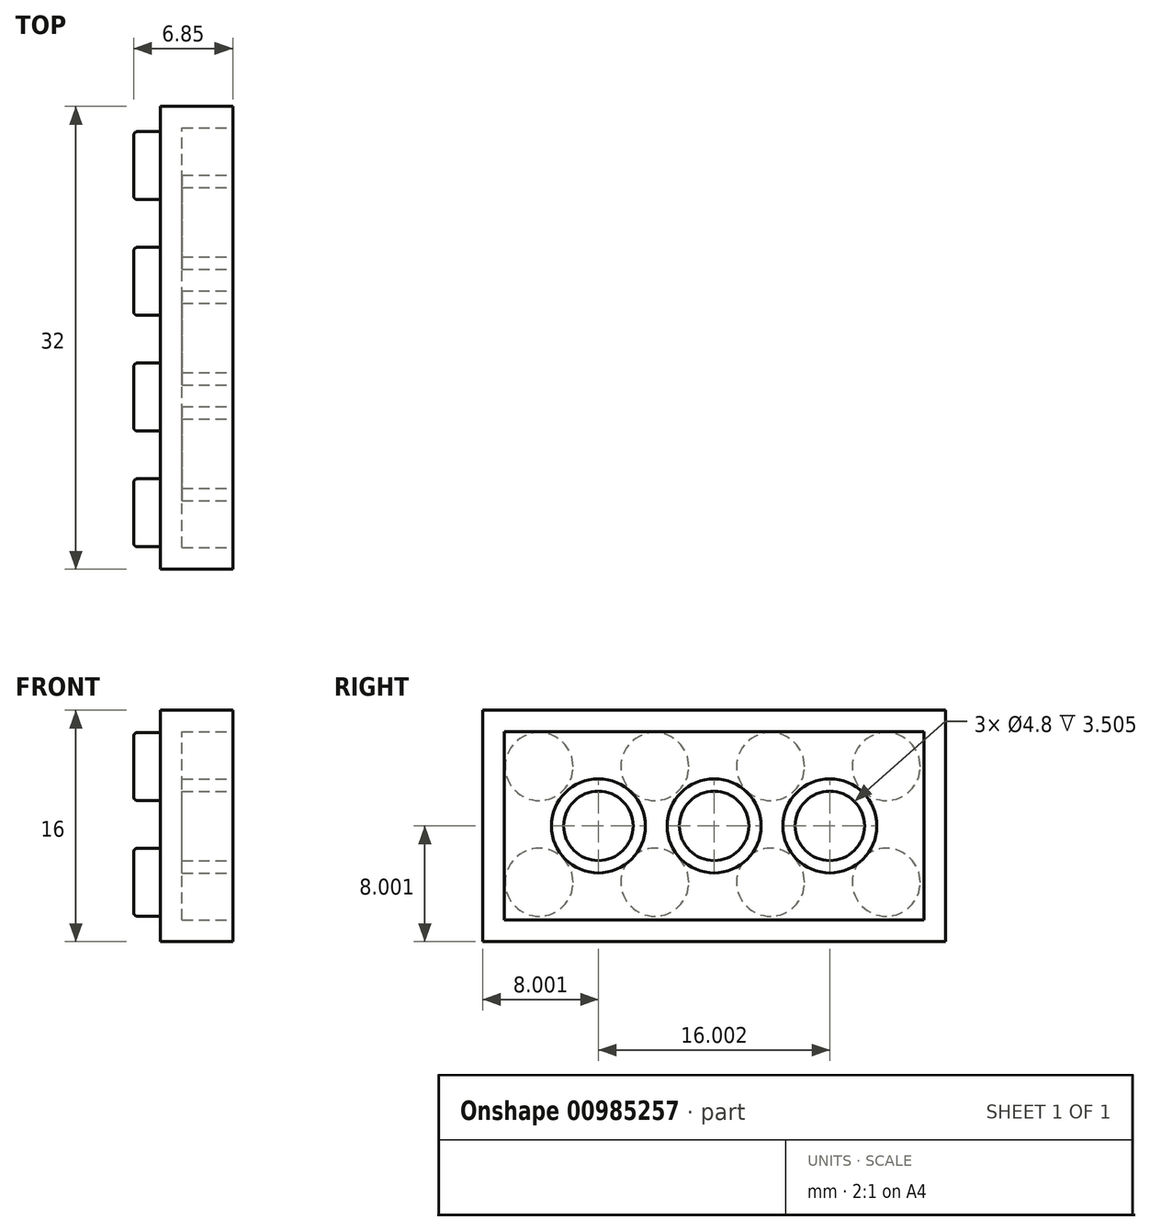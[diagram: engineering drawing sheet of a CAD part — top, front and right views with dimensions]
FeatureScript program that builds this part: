
annotation { "Feature Type Name" : "Feature", "Feature Type Description" : "" }
export const myFeature = defineFeature(function(context is Context, id is Id, definition is map)
    precondition{}
    {
        {
            var Q0;
            Q0=qCreatedBy(makeId("Right.planeOp"),FACE);
            var sketch = newSketch(context, id + "F0", { "sketchPlane" : qUnion([Q0])});
            skLineSegment(sketch, "E0.bottom", {"start": v(0, 0) * mm, "end": v(32, 0) * mm});
            skLineSegment(sketch, "E0.top", {"start": v(0, 16) * mm, "end": v(32, 16) * mm});
            skLineSegment(sketch, "E0.left", {"start": v(0, 0) * mm, "end": v(0, 16) * mm});
            skLineSegment(sketch, "E0.right", {"start": v(32, 0) * mm, "end": v(32, 16) * mm});
            skSolve(sketch);
        }
        {
            var Q0;
            Q0 = qSketchRegion(id + "F0", true);
            extrude(context, id + "F1", {"entities" : qUnion([Q0]), "depth" : 5 * mm, "offsetDistance" : 25.4 * mm});
        }
        {
            var Q0;
            Q0=qCreatedBy(makeId("Right.planeOp"),FACE);
            var sketch = newSketch(context, id + "F2", { "sketchPlane" : qUnion([Q0])});
            skCircle(sketch, "E1", {"center": v(3.9, 12.1) * mm, "radius": 2.35 * mm});
            skCircle(sketch, "E2.1.0.0", {"center": v(11.9, 12.1) * mm, "radius": 2.35 * mm});
            skCircle(sketch, "E2.2.0.0", {"center": v(19.9, 12.1) * mm, "radius": 2.35 * mm});
            skCircle(sketch, "E2.3.0.0", {"center": v(27.9, 12.1) * mm, "radius": 2.35 * mm});
            skLineSegment(sketch, "E2.direction1", {"start": v(3.9, 12.1) * mm, "end": v(11.9, 12.1) * mm, "construction": true});
            skCircle(sketch, "E3.0.1.0", {"center": v(27.9, 4.1) * mm, "radius": 2.35 * mm});
            skCircle(sketch, "E3.0.1.1", {"center": v(19.9, 4.1) * mm, "radius": 2.35 * mm});
            skCircle(sketch, "E3.0.1.2", {"center": v(11.9, 4.1) * mm, "radius": 2.35 * mm});
            skCircle(sketch, "E3.0.1.3", {"center": v(3.9, 4.1) * mm, "radius": 2.35 * mm});
            skLineSegment(sketch, "E3.direction1", {"start": v(27.9, 12.1) * mm, "end": v(53.3, 12.1) * mm, "construction": true});
            skLineSegment(sketch, "E3.direction2", {"start": v(27.9, 12.1) * mm, "end": v(27.9, 4.1) * mm, "construction": true});
            skSolve(sketch);
        }
        {
            var Q0;
            Q0 = qSketchRegion(id + "F2", true);
            extrude(context, id + "F3", {"entities" : qUnion([Q0]), "operationType" : NewBodyOperationType.ADD, "oppositeDirection" : true, "depth" : 1.85 * mm, "offsetDistance" : 25.4 * mm});
        }
        {
            var Q0;
            Q0=makeQuery(id+"F3.opExtrude","CAP_EDGE",EDGE,{"disambiguationData":[OSD([sQuery(id+"F2.wireOp",EDGE,"E3.0.1.0")])],"isStart":false});
            var Q1;
            Q1=makeQuery(id+"F3.opExtrude","CAP_EDGE",EDGE,{"disambiguationData":[OSD([sQuery(id+"F2.wireOp",EDGE,"E2.3.0.0")])],"isStart":false});
            var Q2;
            Q2=makeQuery(id+"F3.opExtrude","CAP_EDGE",EDGE,{"disambiguationData":[OSD([sQuery(id+"F2.wireOp",EDGE,"E2.2.0.0")])],"isStart":false});
            var Q3;
            Q3=makeQuery(id+"F3.opExtrude","CAP_EDGE",EDGE,{"disambiguationData":[OSD([sQuery(id+"F2.wireOp",EDGE,"E3.0.1.1")])],"isStart":false});
            var Q4;
            Q4=makeQuery(id+"F3.opExtrude","CAP_EDGE",EDGE,{"disambiguationData":[OSD([sQuery(id+"F2.wireOp",EDGE,"E3.0.1.2")])],"isStart":false});
            var Q5;
            Q5=makeQuery(id+"F3.opExtrude","CAP_EDGE",EDGE,{"disambiguationData":[OSD([sQuery(id+"F2.wireOp",EDGE,"E2.1.0.0")])],"isStart":false});
            var Q6;
            Q6=makeQuery(id+"F3.opExtrude","CAP_EDGE",EDGE,{"disambiguationData":[OSD([sQuery(id+"F2.wireOp",EDGE,"E1")])],"isStart":false});
            var Q7;
            Q7=makeQuery(id+"F3.opExtrude","CAP_EDGE",EDGE,{"disambiguationData":[OSD([sQuery(id+"F2.wireOp",EDGE,"E3.0.1.3")])],"isStart":false});
            fillet(context, id + "F4", {"entities" : qUnion([Q0, Q1, Q2, Q3, Q4, Q5, Q6, Q7]), "radius" : 0.25 * mm, "tangentPropagation" : true, "allowEdgeOverflow" : false});
        }
        {
            var Q0;
            Q0=makeQuery(id+"F1.opExtrude","CAP_FACE",FACE,{"disambiguationData":[OSD([sQuery(id+"F0.wireOp",EDGE,"E0.bottom"),sQuery(id+"F0.wireOp",EDGE,"E0.top"),sQuery(id+"F0.wireOp",EDGE,"E0.left"),sQuery(id+"F0.wireOp",EDGE,"E0.right")])],"isStart":false});
            var sketch = newSketch(context, id + "F5", { "sketchPlane" : qUnion([Q0])});
            skLineSegment(sketch, "E4.0", {"start": v(1.5, 1.5) * mm, "end": v(30.5, 1.5) * mm});
            skLineSegment(sketch, "E4.1", {"start": v(1.5, 1.5) * mm, "end": v(1.5, 14.5) * mm});
            skLineSegment(sketch, "E4.2", {"start": v(1.5, 14.5) * mm, "end": v(30.5, 14.5) * mm});
            skLineSegment(sketch, "E4.3", {"start": v(30.5, 1.5) * mm, "end": v(30.5, 14.5) * mm});
            skLineSegment(sketch, "E5", {"start": v(32, 0) * mm, "end": v(0, 16) * mm, "construction": true});
            skLineSegment(sketch, "E6", {"start": v(0, 0) * mm, "end": v(32, 16) * mm, "construction": true});
            skCircle(sketch, "E7", {"center": v(16, 8) * mm, "radius": 3.25 * mm});
            skCircle(sketch, "E8", {"center": v(16, 8) * mm, "radius": 2.4 * mm});
            skCircle(sketch, "E9", {"center": v(8, 8) * mm, "radius": 2.4 * mm});
            skCircle(sketch, "E10", {"center": v(8, 8) * mm, "radius": 3.25 * mm});
            skCircle(sketch, "E11", {"center": v(24, 8) * mm, "radius": 2.4 * mm});
            skCircle(sketch, "E12", {"center": v(24, 8) * mm, "radius": 3.25 * mm});
            skSolve(sketch);
        }
        {
            var Q0;
            Q0 = qSketchRegion(id + "F5", true);
            var Q1;
            Q1=makeQuery(id+"F5.imprint","IMPRINT",FACE,{"disambiguationData":[TD([[makeQuery(id+"F5.imprint","IMPRINT",EDGE,{"derivedFrom":sQuery(id+"F5.wireOp",EDGE,"E11")}),1.0]])]});
            var Q2;
            Q2=makeQuery(id+"F5.imprint","IMPRINT",FACE,{"disambiguationData":[TD([[makeQuery(id+"F5.imprint","IMPRINT",EDGE,{"derivedFrom":sQuery(id+"F5.wireOp",EDGE,"E8")}),1.0]])]});
            var Q3;
            Q3=makeQuery(id+"F5.imprint","IMPRINT",FACE,{"disambiguationData":[TD([[makeQuery(id+"F5.imprint","IMPRINT",EDGE,{"derivedFrom":sQuery(id+"F5.wireOp",EDGE,"E9")}),1.0]])]});
            extrude(context, id + "F6", {"entities" : qUnion([Q0, Q1, Q2, Q3]), "operationType" : NewBodyOperationType.REMOVE, "oppositeDirection" : true, "depth" : 3.5 * mm, "offsetDistance" : 25.4 * mm});
        }
    });
